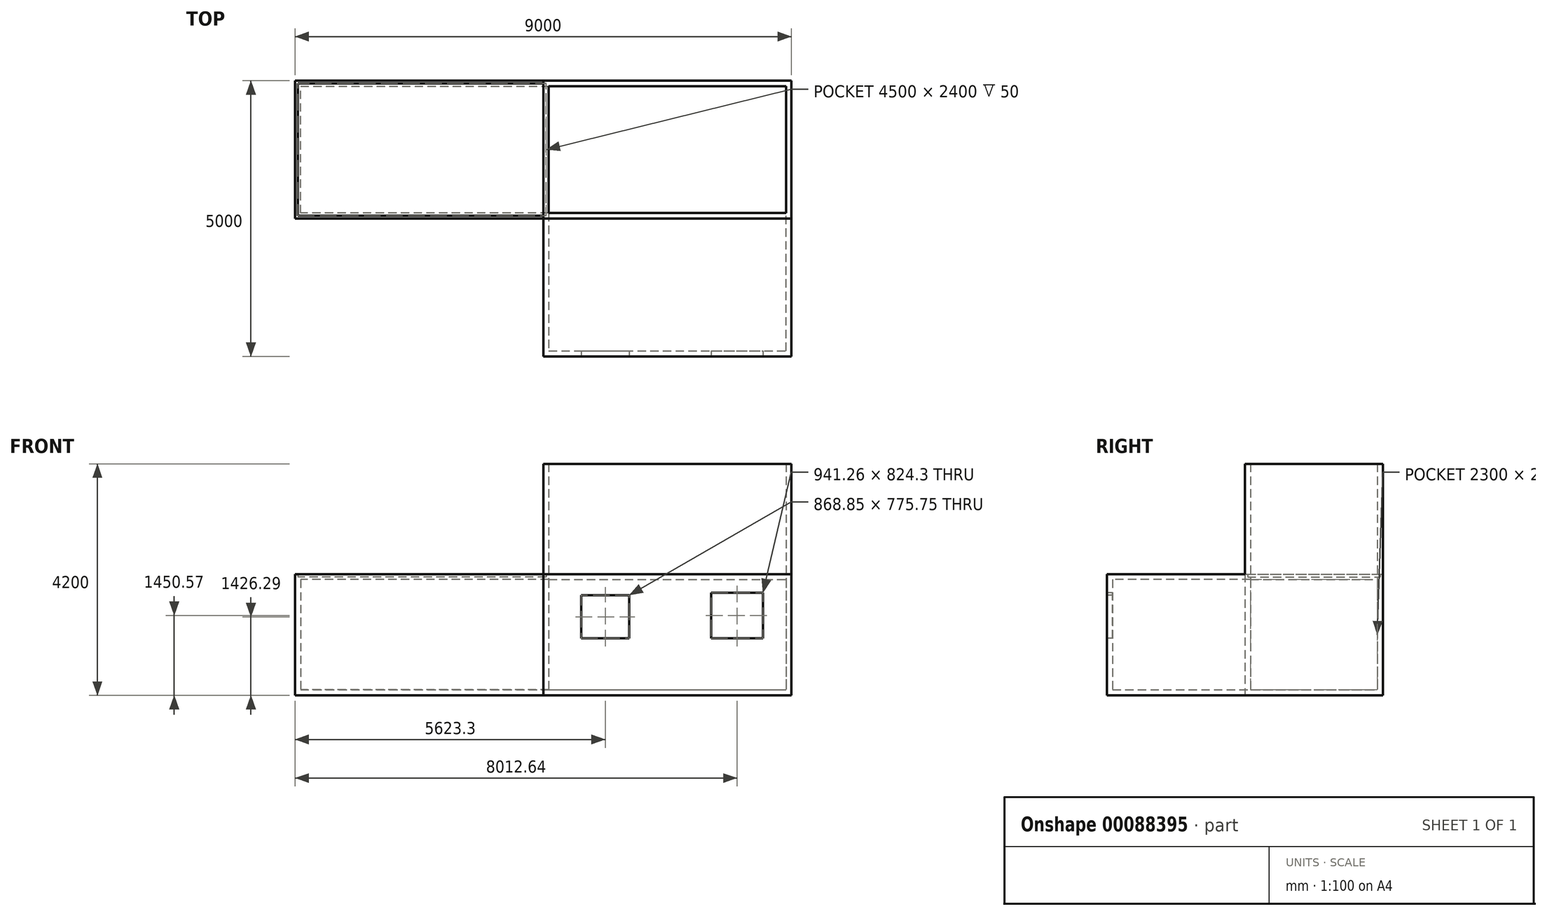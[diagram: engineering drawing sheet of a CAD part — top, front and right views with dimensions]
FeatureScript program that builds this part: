
annotation { "Feature Type Name" : "Feature", "Feature Type Description" : "" }
export const myFeature = defineFeature(function(context is Context, id is Id, definition is map)
    precondition{}
    {
        {
            var Q0;
            Q0=qCreatedBy(makeId("Top.planeOp"),FACE);
            var sketch = newSketch(context, id + "F0", { "sketchPlane" : qUnion([Q0])});
            skLineSegment(sketch, "E0.bottom", {"start": v(0, 0) * mm, "end": v(4500, 0) * mm});
            skLineSegment(sketch, "E0.top", {"start": v(0, 2500) * mm, "end": v(4500, 2500) * mm});
            skLineSegment(sketch, "E0.left", {"start": v(0, 0) * mm, "end": v(0, 2500) * mm});
            skLineSegment(sketch, "E0.right", {"start": v(4500, 0) * mm, "end": v(4500, 2500) * mm});
            skLineSegment(sketch, "E1.top", {"start": v(0, -2500) * mm, "end": v(4500, -2500) * mm});
            skLineSegment(sketch, "E1.left", {"start": v(0, 0) * mm, "end": v(0, -2500) * mm});
            skLineSegment(sketch, "E1.right", {"start": v(4500, 0) * mm, "end": v(4500, -2500) * mm});
            skLineSegment(sketch, "E2.bottom", {"start": v(0, 0) * mm, "end": v(-4500, 0) * mm});
            skLineSegment(sketch, "E2.top", {"start": v(0, 2500) * mm, "end": v(-4500, 2500) * mm});
            skLineSegment(sketch, "E2.right", {"start": v(-4500, 0) * mm, "end": v(-4500, 2500) * mm});
            skSolve(sketch);
        }
        {
            var Q0;
            Q0=makeQuery(id+"F0.imprint","IMPRINT",FACE,{"disambiguationData":[TD([[makeQuery(id+"F0.imprint","IMPRINT",EDGE,{"derivedFrom":sQuery(id+"F0.wireOp",EDGE,"E0.top")}),-1.0]])]});
            extrude(context, id + "F1", {"entities" : qUnion([Q0]), "depth" : 4200 * mm});
        }
        {
            var Q0;
            Q0=makeQuery(id+"F0.imprint","IMPRINT",FACE,{"disambiguationData":[TD([[makeQuery(id+"F0.imprint","IMPRINT",EDGE,{"derivedFrom":sQuery(id+"F0.wireOp",EDGE,"E0.bottom")}),-1.0]])]});
            extrude(context, id + "F2", {"entities" : qUnion([Q0]), "operationType" : NewBodyOperationType.ADD, "depth" : 2200 * mm});
        }
        {
            var Q0;
            Q0=makeQuery(id+"F0.imprint","IMPRINT",FACE,{"disambiguationData":[TD([[makeQuery(id+"F0.imprint","IMPRINT",EDGE,{"derivedFrom":sQuery(id+"F0.wireOp",EDGE,"E2.bottom")}),-1.0]])]});
            extrude(context, id + "F3", {"entities" : qUnion([Q0]), "operationType" : NewBodyOperationType.ADD, "depth" : 2200 * mm});
        }
        {
            var Q0;
            Q0=makeQuery(id+"F1.opExtrude","CAP_FACE",FACE,{"disambiguationData":[OSD([sQuery(id+"F0.wireOp",EDGE,"E0.top"),sQuery(id+"F0.wireOp",EDGE,"E0.right"),sQuery(id+"F0.wireOp",EDGE,"E0.bottom"),sQuery(id+"F0.wireOp",EDGE,"E0.left")])],"isStart":false});
            shell(context, id + "F4", {"entities" : qUnion([Q0]), "thickness" : 100 * mm});
        }
        {
            var Q0;
            Q0=makeQuery(id+"F3.opExtrude","CAP_FACE",FACE,{"disambiguationData":[OSD([sQuery(id+"F0.wireOp",EDGE,"E2.bottom"),sQuery(id+"F0.wireOp",EDGE,"E2.top"),sQuery(id+"F0.wireOp",EDGE,"E0.left"),sQuery(id+"F0.wireOp",EDGE,"E2.right")])],"isStart":false});
            shell(context, id + "F5", {"entities" : qUnion([Q0]), "thickness" : 50 * mm});
        }
        {
            var Q0;
            Q0=makeQuery(id+"F2.opExtrude","SWEPT_FACE",FACE,{"disambiguationData":[OSD([sQuery(id+"F0.wireOp",EDGE,"E1.top")])]});
            var sketch = newSketch(context, id + "F6", { "sketchPlane" : qUnion([Q0])});
            skLineSegment(sketch, "E3.bottom", {"start": v(688.87, 1038.41) * mm, "end": v(1557.72, 1038.41) * mm});
            skLineSegment(sketch, "E3.top", {"start": v(688.87, 1814.16) * mm, "end": v(1557.72, 1814.16) * mm});
            skLineSegment(sketch, "E3.left", {"start": v(688.87, 1038.41) * mm, "end": v(688.87, 1814.16) * mm});
            skLineSegment(sketch, "E3.right", {"start": v(1557.72, 1038.41) * mm, "end": v(1557.72, 1814.16) * mm});
            skLineSegment(sketch, "E4.bottom", {"start": v(3042.01, 1038.41) * mm, "end": v(3983.27, 1038.41) * mm});
            skLineSegment(sketch, "E4.top", {"start": v(3042.01, 1862.72) * mm, "end": v(3983.27, 1862.72) * mm});
            skLineSegment(sketch, "E4.left", {"start": v(3042.01, 1038.41) * mm, "end": v(3042.01, 1862.72) * mm});
            skLineSegment(sketch, "E4.right", {"start": v(3983.27, 1038.41) * mm, "end": v(3983.27, 1862.72) * mm});
            skSolve(sketch);
        }
        {
            var Q0;
            Q0=makeQuery(id+"F6.imprint","IMPRINT",FACE,{"disambiguationData":[TD([[makeQuery(id+"F6.imprint","IMPRINT",EDGE,{"derivedFrom":sQuery(id+"F6.wireOp",EDGE,"E3.bottom")}),1.0]])]});
            var Q1;
            Q1=makeQuery(id+"F6.imprint","IMPRINT",FACE,{"disambiguationData":[TD([[makeQuery(id+"F6.imprint","IMPRINT",EDGE,{"derivedFrom":sQuery(id+"F6.wireOp",EDGE,"E4.bottom")}),1.0]])]});
            extrude(context, id + "F7", {"entities" : qUnion([Q0, Q1]), "operationType" : NewBodyOperationType.REMOVE, "endBound" : BoundingType.UP_TO_NEXT, "oppositeDirection" : true, "depth" : 25 * mm});
        }
    });
